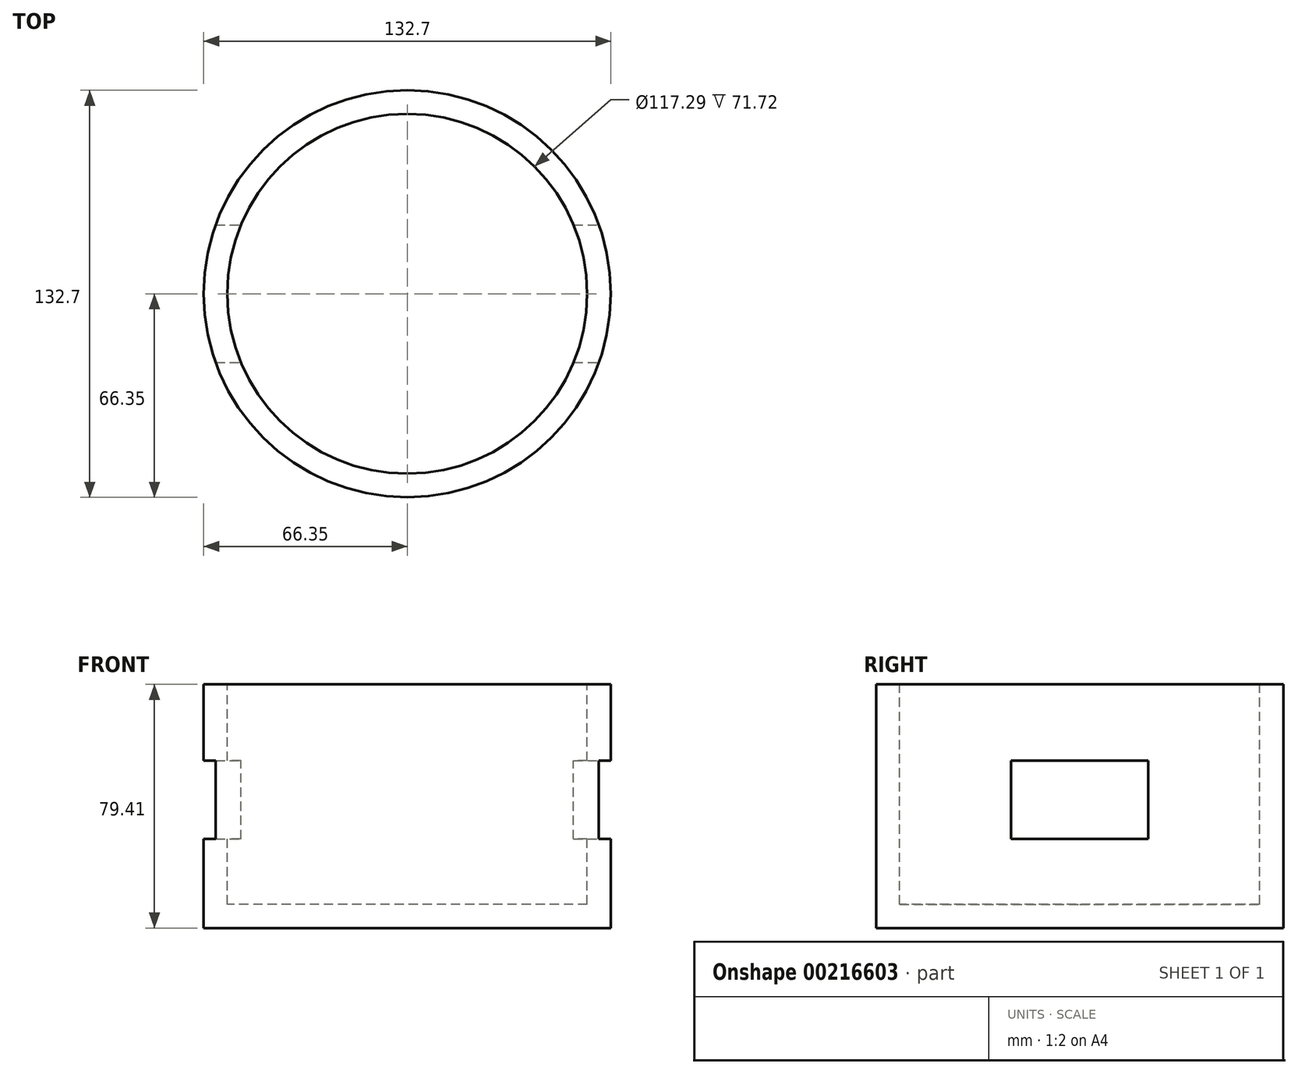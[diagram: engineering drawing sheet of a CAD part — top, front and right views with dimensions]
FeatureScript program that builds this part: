
annotation { "Feature Type Name" : "Feature", "Feature Type Description" : "" }
export const myFeature = defineFeature(function(context is Context, id is Id, definition is map)
    precondition{}
    {
        {
            var Q0;
            Q0=qCreatedBy(makeId("Front.planeOp"),FACE);
            var sketch = newSketch(context, id + "F0", { "sketchPlane" : qUnion([Q0])});
            skLineSegment(sketch, "E0", {"start": v(0, 0) * mm, "end": v(66.35, 0) * mm});
            skLineSegment(sketch, "E1", {"start": v(66.35, 0) * mm, "end": v(66.35, 79.4) * mm});
            skLineSegment(sketch, "E2", {"start": v(66.35, 79.4) * mm, "end": v(58.65, 79.4) * mm});
            skLineSegment(sketch, "E3", {"start": v(58.65, 79.4) * mm, "end": v(58.65, 7.69) * mm});
            skLineSegment(sketch, "E4", {"start": v(58.65, 7.69) * mm, "end": v(0, 7.69) * mm});
            skLineSegment(sketch, "E5", {"start": v(0, 7.69) * mm, "end": v(0, 0) * mm});
            skSolve(sketch);
        }
        {
            var Q0;
            Q0=makeQuery(id+"F0.imprint","IMPRINT",FACE,{"disambiguationData":[TD([[makeQuery(id+"F0.imprint","IMPRINT",EDGE,{"derivedFrom":sQuery(id+"F0.wireOp",EDGE,"E0")}),1.0]])]});
            var Q1;
            Q1=sQuery(id+"F0.wireOp",EDGE,"E5");
            revolve(context, id + "F1", {"entities" : qUnion([Q0]), "axis" : qUnion([Q1]), "revolveType" : RevolveType.FULL});
        }
        {
            var Q0;
            Q0=qCreatedBy(makeId("Right.planeOp"),FACE);
            var sketch = newSketch(context, id + "F2", { "sketchPlane" : qUnion([Q0])});
            skLineSegment(sketch, "E6.bottom", {"start": v(-22.4, 29.01) * mm, "end": v(22.4, 29.01) * mm});
            skLineSegment(sketch, "E6.top", {"start": v(-22.4, 54.52) * mm, "end": v(22.4, 54.52) * mm});
            skLineSegment(sketch, "E6.left", {"start": v(-22.4, 29.01) * mm, "end": v(-22.4, 54.52) * mm});
            skLineSegment(sketch, "E6.right", {"start": v(22.4, 29.01) * mm, "end": v(22.4, 54.52) * mm});
            skPoint(sketch, "E6.middle", {"position": v(0, 41.77) * mm});
            skSolve(sketch);
        }
        {
            var Q0;
            Q0=makeQuery(id+"F2.imprint","IMPRINT",FACE,{"disambiguationData":[TD([[makeQuery(id+"F2.imprint","IMPRINT",EDGE,{"derivedFrom":sQuery(id+"F2.wireOp",EDGE,"E6.bottom")}),1.0]])]});
            extrude(context, id + "F3", {"entities" : qUnion([Q0]), "operationType" : NewBodyOperationType.REMOVE, "endBound" : BoundingType.SYMMETRIC, "oppositeDirection" : true, "depth" : 194.56 * mm});
        }
    });
